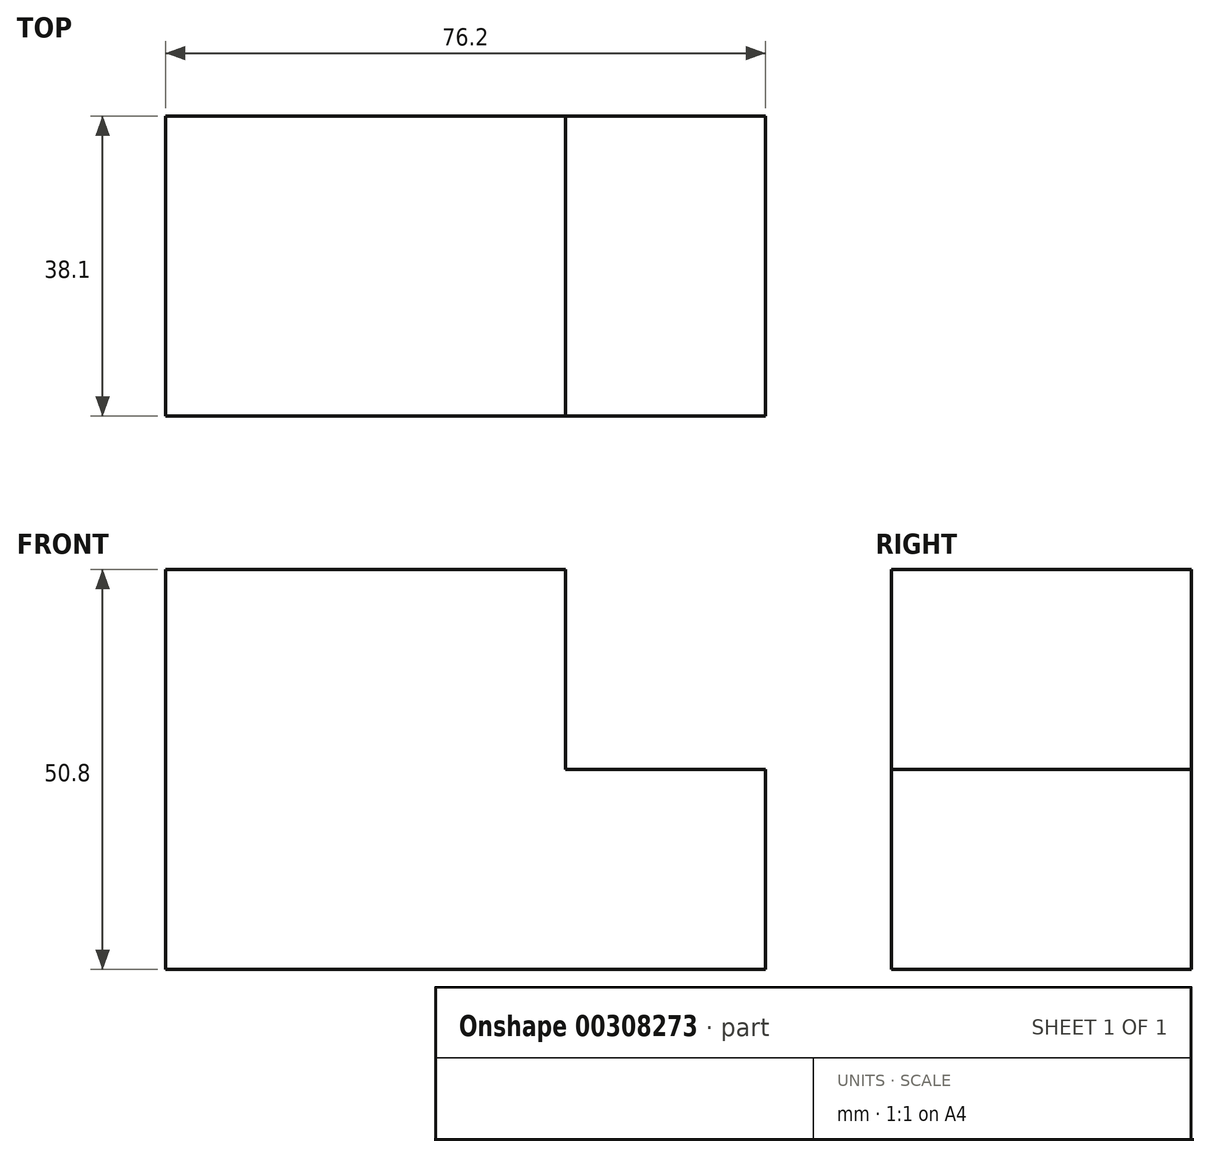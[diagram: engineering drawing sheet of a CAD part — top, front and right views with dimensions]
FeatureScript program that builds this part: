
annotation { "Feature Type Name" : "Feature", "Feature Type Description" : "" }
export const myFeature = defineFeature(function(context is Context, id is Id, definition is map)
    precondition{}
    {
        {
            var Q0;
            Q0=qCreatedBy(makeId("Front.planeOp"),FACE);
            var sketch = newSketch(context, id + "F0", { "sketchPlane" : qUnion([Q0])});
            skLineSegment(sketch, "E0", {"start": v(-41.1, -41.83) * mm, "end": v(35.1, -41.83) * mm});
            skLineSegment(sketch, "E1", {"start": v(35.1, -41.83) * mm, "end": v(35.1, -16.43) * mm});
            skLineSegment(sketch, "E2", {"start": v(35.1, -16.43) * mm, "end": v(9.7, -16.43) * mm});
            skLineSegment(sketch, "E3", {"start": v(9.7, -16.43) * mm, "end": v(9.7, 8.97) * mm});
            skLineSegment(sketch, "E4", {"start": v(9.7, 8.97) * mm, "end": v(-41.1, 8.97) * mm});
            skLineSegment(sketch, "E5", {"start": v(-41.1, 8.97) * mm, "end": v(-41.1, -41.83) * mm});
            skSolve(sketch);
        }
        {
            var Q0;
            Q0=makeQuery(id+"F0.imprint","IMPRINT",FACE,{"disambiguationData":[TD([[makeQuery(id+"F0.imprint","IMPRINT",EDGE,{"derivedFrom":sQuery(id+"F0.wireOp",EDGE,"E0")}),1.0]])]});
            extrude(context, id + "F1", {"entities" : qUnion([Q0]), "depth" : 38.1 * mm});
        }
    });
